# Revit family: UCS Retrofit
name_source: partatom
category: Lighting Fixtures
revit_build: Autodesk Revit Architecture 2012 (Build: 20110309_2315(x64)
units: mm (PartAtom-declared; Revit-internal decimal feet)

## types (5) — shared parameters
Assembly Code = D5020200
Description = Lighting Fixture
Frequency = 60 Hz
Full Load Current = 1 A
Glass Material = Glass-AAL-Acrylic
Housing Material = Aluminum-AAL-Artic White
Housing Radius = 2.754 "
LEED = www.usgbc.org
Manufacturer = Architectural Area Lighting
MasterFormat Number = 26.56.29
MasterFormat Title = Area Lighting
Model = UCS
Note Text = LF
Note Visible = Yes
Number of Poles = 1
OmniClass Number = 23.80.70.14.11.14
OmniClass Title = Post-Top Lighting
Photometric Web = Web UCS : UCS-FLR-70MH-FCO
Power Factor = 1
Revision Date = 02/22/2010
Series = Universe
URL = www.aal.net
Voltage = 120 V
zero-valued in all types: Default elevation

## per-type parameters (varying)
| type | Apparent Load | Architectural Design Manual | External Housing Radius | Flared Hood | Housing Height | Lamp | Skirted Bell Hood | Straight Hood | Type Comments | Wattage Comments |
| 13" ø FLR 70 Watt MH-FCO | 70 VA | www.aal.net/sections/downloads/html/downloads.html | 7.5 " | Yes | 13 " | Metal Halide | No | No | with opal glass lens | 70 watt medium base clear ED-17 HM lamp |
| 16" ø SKB 70 Watt MH-FCO | 70 VA | www.aal.net/sections/downloads/html/downloads.html | 7.5 " | No | 16 " | Metal Halide | Yes | No | with skirted bell hood, full cutoff | 70 watt medium base clear ED-17 HM lamp |
| 16" ø STR 42 Watt CFL | 42 VA | www.aal.net/sections/downloads/html/downloads.html | 8 " | No | 12.684 " | Compact Fluorescent | No | Yes | on relamp door | 42 watt CFL |
| 16" ø STR 70 Watt MH | 70 VA | www.aal.net/sections/downloads/html/downloads.html | 8 " | No | 12.684 " | Metal Halide | No | Yes | on relamp door | 70 watt medium base clear E-17 MH |
| 16" ø STR 70 Watt MH-FCO | 70 VA | http://cdn.aal.net | 8 " | No | 12.684 " | Metal Halide | No | Yes | on relamp door. full cutoff | 70 watt medium base clear ED-17 MH |

## geometry (parser evidence)
native form markers: Blend x38, Sweep x4
no freeform markers — native parametric forms only
